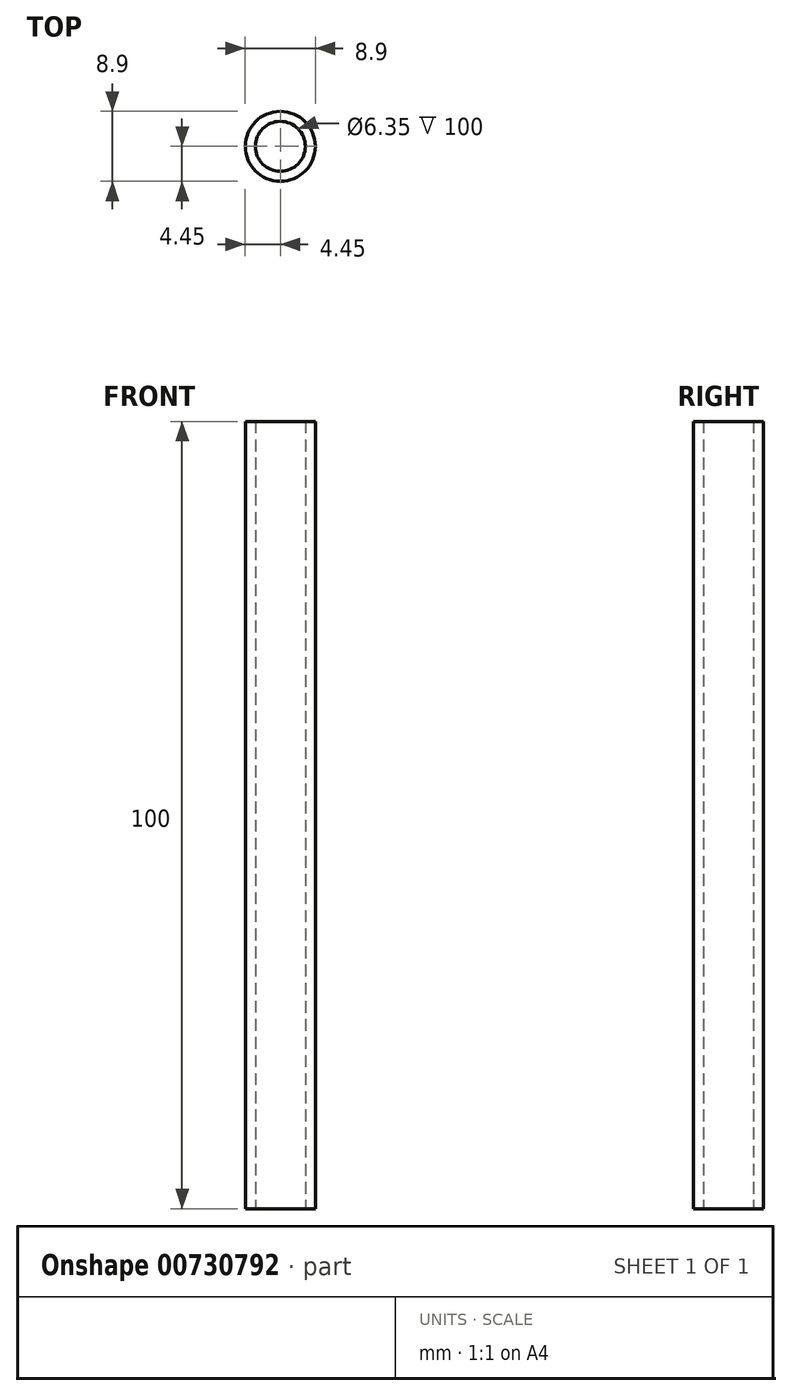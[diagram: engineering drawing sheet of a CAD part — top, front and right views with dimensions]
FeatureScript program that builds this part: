
annotation { "Feature Type Name" : "Feature", "Feature Type Description" : "" }
export const myFeature = defineFeature(function(context is Context, id is Id, definition is map)
    precondition{}
    {
        {
            var Q0;
            Q0=qCreatedBy(makeId("Top.planeOp"),FACE);
            var sketch = newSketch(context, id + "F0", { "sketchPlane" : qUnion([Q0])});
            skCircle(sketch, "E0", {"center": v(0, 0) * mm, "radius": 3.18 * mm});
            skCircle(sketch, "E1", {"center": v(0, 0) * mm, "radius": 4.45 * mm});
            skSolve(sketch);
        }
        {
            var Q0;
            Q0=makeQuery(id+"F0.imprint","IMPRINT",FACE,{"disambiguationData":[TD([[makeQuery(id+"F0.imprint","IMPRINT",EDGE,{"derivedFrom":sQuery(id+"F0.wireOp",EDGE,"E0")}),-1.0]])]});
            extrude(context, id + "F1", {"entities" : qUnion([Q0]), "depth" : 100 * mm, "offsetDistance" : 25 * mm});
        }
    });
